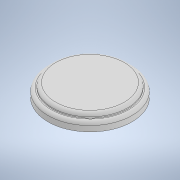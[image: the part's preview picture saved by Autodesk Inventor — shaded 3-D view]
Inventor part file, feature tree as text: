
AUTODESK INVENTOR PART (.ipt)
format: ipt  version: 2022 (Build 260153000, 153)  size: 131,584 bytes
history: native  units: mm
features: revolve x1, fillet x1, sketch x1
ambient origin geometry x8: Origin, YZ Plane, XZ Plane, XY Plane, X Axis, Y Axis, Z Axis, Center Point
bodies: Solid1 (feature_tree)
feature tree (3):
  revolve  "Revolution1"  [1 undecoded]
  fillet  "Fillet1"  Radius=1.0mm
  sketch  "Sketch1"  dims[d0=9.525mm d1=2.0mm d2=1.0mm d3=1.0mm d4=90.0deg d5=0.75mm]
note: 1 required parameter value undecoded (feature->parameter linkage not recoverable at this tier; creation-order binding heuristic only, values carry confidence <= 0.55)
